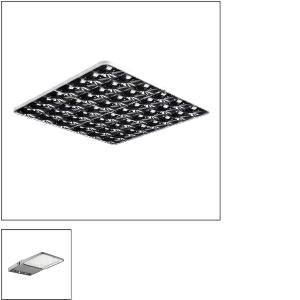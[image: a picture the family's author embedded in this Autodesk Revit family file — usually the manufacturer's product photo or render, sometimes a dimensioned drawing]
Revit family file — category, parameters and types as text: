
# Revit family: siteco_mirrortec_r__indoor___rs05_5nw14091qa_1e52
name_source: partatom
category: Lighting Fixtures
units: mm (PartAtom-declared; Revit-internal decimal feet)

## family parameters
Cut with Voids When Loaded = No
Host = Face
Light Source = No
Part Type = Normal
Room Calculation Point = No
Round Connector Dimension = Use Diameter
Shared = No

## types (1)
- 5XA7682G2H2AC (1 x LED, 34300 lm, 305.7 W, 4000K)
    Apparent Load = 306 VA
    CIE Flux Codes = 47 83 98 49 100
    Color Rendering = 70
    Color Temperature = 4000K
    Default Elevation = 1800 mm
    Description = secondary reflector, for Siteco Mirrortec® Indoor, ball-and-socket joint pendant suspension, housing, square, of aluminium, coated, metallic grey (RAL 9006), fresnel reflector 100, of PMMA, aluminized, highly specular, light point resolution, fresnel structure, length: 600 mm, width: 600 mm

Light Distribution: RS05
    Height = 342 mm
    Lamp = 1 x LED
    Lamp Light Flux = 34300 lm
    Lamp Power = 305.7 W
    Lamp count = 1
    Length = 618 mm
    Luminous efficacy = 112 lm/W
    Manufacturer = Siteco
    ModVariant = No
    Model = 5NW14091QA
    Mounting Place = Ceiling
    Mounting Type = Pendant
    Number of Poles = 1
    OnlyDefault = Yes
    Power Factor = 1
    Product Name = Siteco Mirrortec® Indoor | RS05
    Product group = secondary reflector
    ProductGroupID = 908
    Protection Class = Protection class II
    Protection Degree = IP 66
    RLX_Detail_Level = 1
    RLX_Emergency_Light_Flux = 0 lm
    RLX_Emergency_Type = 0
    RLX_Emergency_Type_DB = No
    RlxData = <blob elided: 104305 chars, md5=e012fa29>
    Socket = socket
    Standby Power = 0 W
    System Light Flux = 34300 lm
    System Power = 306 W
    Type Comments = Floodlight FL 20 midi, floodlight, primary light control with lens, of plastic, primary optical cover: protective disc, of toughened safety glass, transparent, light distribution: RS05, light emission: direct distribution, primary light characteristic: rotationally symmetric, installation type: surface-mounted, LED, High Power LED, rated luminous flux: 38.380lm, luminous efficacy: 126lm/W, light colour: 740, colour temperature: 4000K, control gear: ECG Plus, control: overheat protection, power reduction, digital communication interface, time-dependent luminous flux control, flexible luminous flux parameterisation, electronic power reduction, with terminal, 10-pole, max. 2.5mm², mains connection: 220..240V, AC, 50/60Hz, rated input power: 306W, LED unit, of diecast aluminium, powder-coated, Siteco® metallic grey (DB 702S), corrosivity category C5 mid according to DIN EN ISO 12944, length: 731mm, width: 450mm, height: 76mm, housing frame, of diecast aluminium, powder-coated, Siteco® metallic grey (DB 702S), wall fastening, DALI, protection rating (complete): IP66, insulation class (complete): insulation class II (safety insulation), certification: CE, ENEC, VDE, protection symbol: D, permissible operating ambient temperature: -40..+40°C, permissible operating ambient temperature for outdoor applications: -40..+50°C, standard: DIN EN 12944, packaging unit: 1 piece

individual setting: distance floodlight mirror = 2,0m / reflector tilt = 5°
    Type Image = l_577132_1005944.jpg
    URL = http://relux.com
    VarID = 5xa7682g2h2ac@adj_135749
    Voltage = 0 V
    Weight = 0.00 kg
    Width = 618 mm

## geometry (parser evidence)
native form markers: Blend x4, Sweep x11
no freeform markers — native parametric forms only
